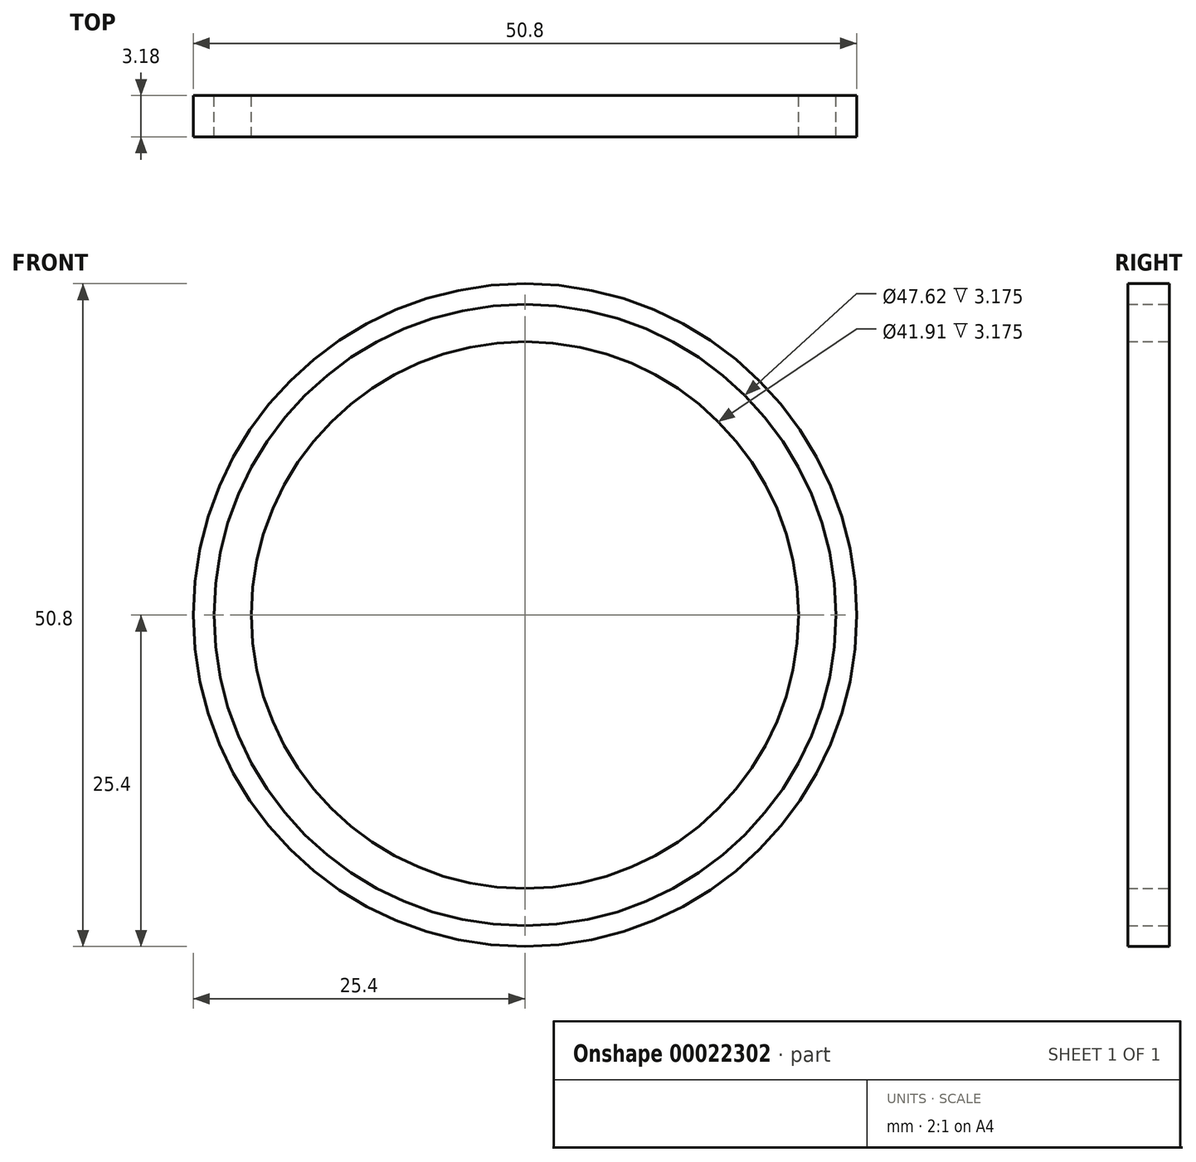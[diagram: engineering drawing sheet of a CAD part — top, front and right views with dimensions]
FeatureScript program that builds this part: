
annotation { "Feature Type Name" : "Feature", "Feature Type Description" : "" }
export const myFeature = defineFeature(function(context is Context, id is Id, definition is map)
    precondition{}
    {
        {
            var Q0;
            Q0=qCreatedBy(makeId("Front.planeOp"),FACE);
            var sketch = newSketch(context, id + "F0", { "sketchPlane" : qUnion([Q0])});
            skCircle(sketch, "E0", {"center": v(0, 0) * mm, "radius": 25.4 * mm});
            skCircle(sketch, "E1", {"center": v(0, 0) * mm, "radius": 23.81 * mm});
            skSolve(sketch);
        }
        {
            var Q0;
            Q0=sQuery(id+"F0.wireOp",EDGE,"E0");
            extrude(context, id + "F1", {"bodyType" : ToolBodyType.SURFACE, "surfaceEntities" : qUnion([Q0]), "depth" : 3.17 * mm});
        }
        {
            var Q0;
            Q0=qCreatedBy(makeId("Front.planeOp"),FACE);
            var sketch = newSketch(context, id + "F2", { "sketchPlane" : qUnion([Q0])});
            skCircle(sketch, "E2", {"center": v(0, 0) * mm, "radius": 25.4 * mm});
            skCircle(sketch, "E3", {"center": v(0, 0) * mm, "radius": 20.96 * mm});
            skSolve(sketch);
        }
        {
            var Q0;
            Q0 = qSketchRegion(id + "F2", true);
            var Q1;
            Q1 = qSketchRegion(id + "F0", true);
            extrude(context, id + "F3", {"entities" : qUnion([Q0, Q1]), "depth" : 3.17 * mm});
        }
    });
